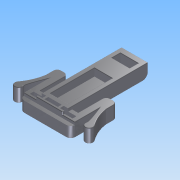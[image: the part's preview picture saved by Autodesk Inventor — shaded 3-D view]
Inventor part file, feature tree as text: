
AUTODESK INVENTOR PART (.ipt)
format: ipt  version: 2015 SP1 (Build 190203100, 203)  size: 534,528 bytes
history: native  units: mm
features: extrude x7, sketch x6, fillet x5, other x2
ambient origin geometry x8: Origin, YZ Plane, XZ Plane, XY Plane, X Axis, Y Axis, Z Axis, Center Point
bodies: Body1 (feature_tree)
feature tree (20):
  other  "Твердое тело1"
  extrude  "Выдавливание1"  Depth=28.5mm
  fillet  "Сопряжение2"  Radius=33.5mm
  extrude  "Выдавливание2"  Depth=1.5mm
  extrude  "Выдавливание3"  Depth=4.9mm
  extrude  "Выдавливание4"  Depth=1.7mm
  extrude  "Выдавливание5"  Depth=5.0mm TaperAngle=0.0deg
  extrude  "Выдавливание6"  Depth=2.0mm
  extrude  "Выдавливание7"  Depth=1.0mm TaperAngle=0.0deg
  fillet  "Сопряжение3"  Radius=1.0mm
  fillet  "Сопряжение4"  Radius=0.75mm
  fillet  "Сопряжение5"  Radius=1.0mm
  fillet  "Сопряжение6"  Radius=0.75mm
  other  "Картинка2"
  sketch  "Эскиз3"
  sketch  "Эскиз4"
  sketch  "Эскиз6"
  sketch  "Эскиз7"
  sketch  "Эскиз8"
  sketch  "Эскиз9"
